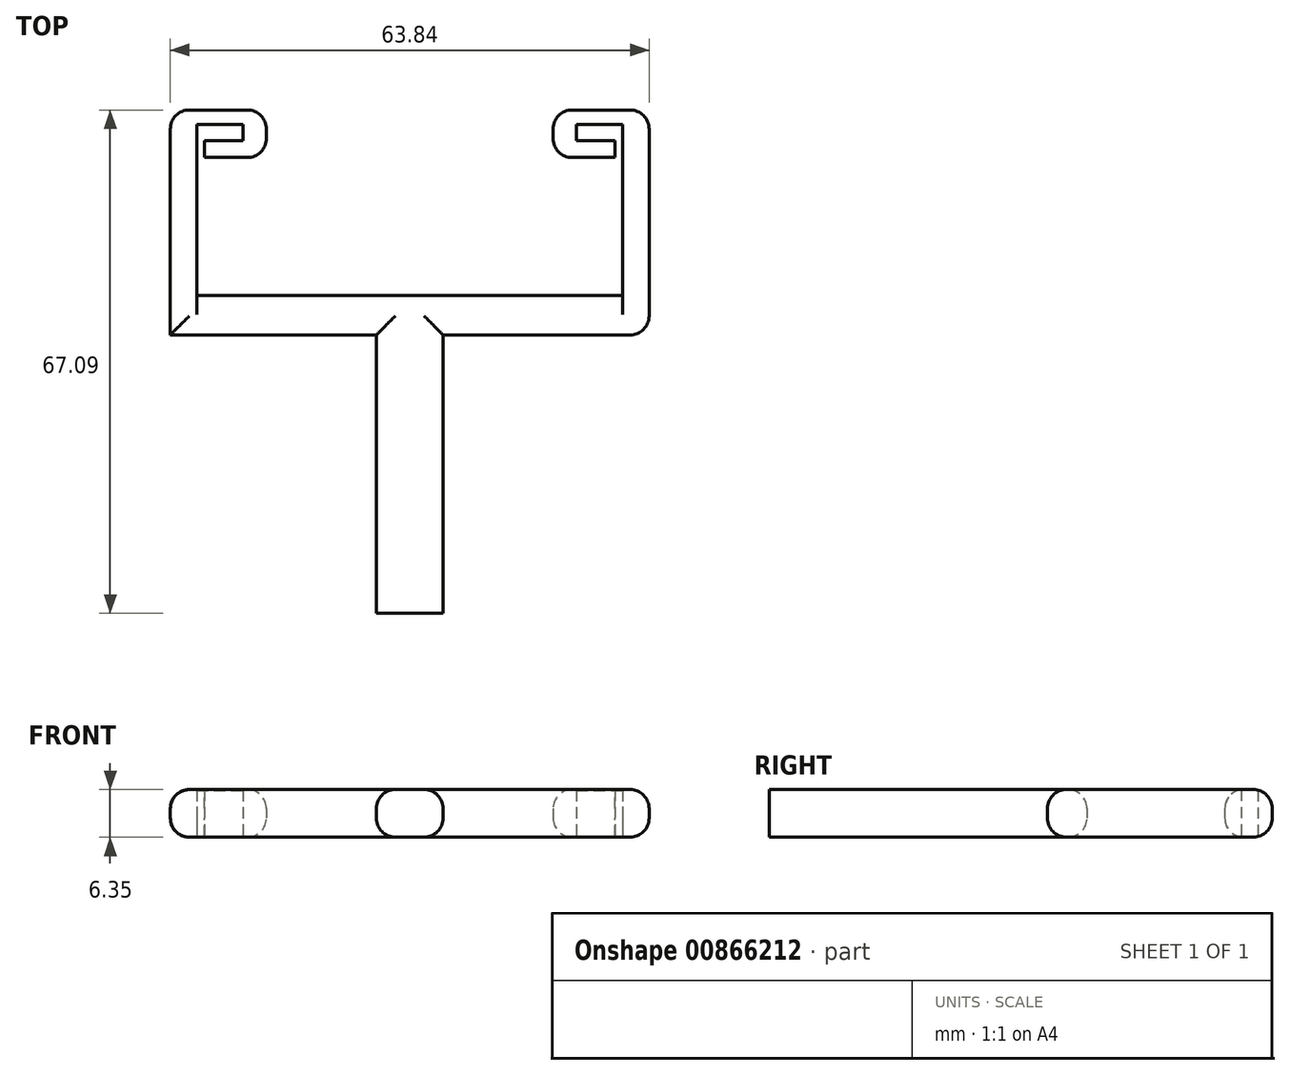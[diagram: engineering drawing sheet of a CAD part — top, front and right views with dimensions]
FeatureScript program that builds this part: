
annotation { "Feature Type Name" : "Feature", "Feature Type Description" : "" }
export const myFeature = defineFeature(function(context is Context, id is Id, definition is map)
    precondition{}
    {
        {
            var Q0;
            Q0=qCreatedBy(makeId("Top.planeOp"),FACE);
            var sketch = newSketch(context, id + "F0", { "sketchPlane" : qUnion([Q0])});
            skLineSegment(sketch, "E0.bottom", {"start": v(0, -33.38) * mm, "end": v(-4.45, -33.38) * mm});
            skLineSegment(sketch, "E0.top", {"start": v(0, 9) * mm, "end": v(-4.45, 9) * mm});
            skLineSegment(sketch, "E0.right", {"start": v(-4.45, -33.38) * mm, "end": v(-4.45, 3.72) * mm});
            skLineSegment(sketch, "E1.bottom", {"start": v(-4.45, 9) * mm, "end": v(-28.38, 9) * mm});
            skLineSegment(sketch, "E1.top", {"start": v(-4.45, 3.72) * mm, "end": v(-31.92, 3.72) * mm});
            skLineSegment(sketch, "E1.right", {"start": v(-31.92, 9) * mm, "end": v(-31.92, 3.72) * mm});
            skLineSegment(sketch, "E2.top", {"start": v(-31.92, 33.7) * mm, "end": v(-28.38, 33.7) * mm});
            skLineSegment(sketch, "E2.left", {"start": v(-31.92, 9) * mm, "end": v(-31.92, 33.7) * mm});
            skLineSegment(sketch, "E2.right", {"start": v(-28.38, 9) * mm, "end": v(-28.38, 31.8) * mm});
            skLineSegment(sketch, "E3.bottom", {"start": v(-19.1, 33.7) * mm, "end": v(-28.38, 33.7) * mm});
            skLineSegment(sketch, "E3.top", {"start": v(-22.24, 31.8) * mm, "end": v(-28.38, 31.8) * mm});
            skLineSegment(sketch, "E3.left", {"start": v(-19.1, 33.7) * mm, "end": v(-19.1, 31.8) * mm});
            skLineSegment(sketch, "E4.top", {"start": v(-19.1, 27.38) * mm, "end": v(-22.24, 27.38) * mm});
            skLineSegment(sketch, "E4.left", {"start": v(-19.1, 31.8) * mm, "end": v(-19.1, 27.38) * mm});
            skLineSegment(sketch, "E4.right", {"start": v(-22.24, 31.8) * mm, "end": v(-22.24, 29.6) * mm});
            skLineSegment(sketch, "E5.bottom", {"start": v(-27.34, 27.38) * mm, "end": v(-22.24, 27.38) * mm});
            skLineSegment(sketch, "E5.top", {"start": v(-27.34, 29.6) * mm, "end": v(-22.24, 29.6) * mm});
            skLineSegment(sketch, "E5.left", {"start": v(-27.34, 27.38) * mm, "end": v(-27.34, 29.6) * mm});
            skLineSegment(sketch, "E6.MirrorCS", {"start": v(4.45, -33.38) * mm, "end": v(4.45, 3.72) * mm});
            skLineSegment(sketch, "E7.MirrorCS", {"start": v(0, 9) * mm, "end": v(4.45, 9) * mm});
            skLineSegment(sketch, "E8.MirrorCS", {"start": v(4.45, 3.72) * mm, "end": v(31.92, 3.72) * mm});
            skLineSegment(sketch, "E9.MirrorCS", {"start": v(4.45, 9) * mm, "end": v(28.38, 9) * mm});
            skLineSegment(sketch, "E10.MirrorCS", {"start": v(28.38, 9) * mm, "end": v(28.38, 31.8) * mm});
            skLineSegment(sketch, "E11.MirrorCS", {"start": v(31.92, 9) * mm, "end": v(31.92, 33.7) * mm});
            skLineSegment(sketch, "E12.MirrorCS", {"start": v(19.1, 33.7) * mm, "end": v(28.38, 33.7) * mm});
            skLineSegment(sketch, "E13.MirrorCS", {"start": v(31.92, 33.7) * mm, "end": v(28.38, 33.7) * mm});
            skLineSegment(sketch, "E14.MirrorCS", {"start": v(19.1, 31.8) * mm, "end": v(19.1, 27.38) * mm});
            skLineSegment(sketch, "E15.MirrorCS", {"start": v(22.24, 31.8) * mm, "end": v(28.38, 31.8) * mm});
            skLineSegment(sketch, "E16.MirrorCS", {"start": v(27.34, 29.6) * mm, "end": v(22.24, 29.6) * mm});
            skLineSegment(sketch, "E17.MirrorCS", {"start": v(27.34, 27.38) * mm, "end": v(27.34, 29.6) * mm});
            skLineSegment(sketch, "E18.MirrorCS", {"start": v(27.34, 27.38) * mm, "end": v(22.24, 27.38) * mm});
            skLineSegment(sketch, "E19.MirrorCS", {"start": v(19.1, 27.38) * mm, "end": v(22.24, 27.38) * mm});
            skLineSegment(sketch, "E20.MirrorCS", {"start": v(22.24, 31.8) * mm, "end": v(22.24, 29.6) * mm});
            skLineSegment(sketch, "E21.MirrorCS", {"start": v(19.1, 33.7) * mm, "end": v(19.1, 31.8) * mm});
            skLineSegment(sketch, "E22.MirrorCS", {"start": v(31.92, 9) * mm, "end": v(31.92, 3.72) * mm});
            skLineSegment(sketch, "E23.MirrorCS", {"start": v(0, -33.38) * mm, "end": v(4.45, -33.38) * mm});
            skSolve(sketch);
        }
        {
            var Q0;
            Q0=makeQuery(id+"F0.imprint","IMPRINT",FACE,{"disambiguationData":[TD([[makeQuery(id+"F0.imprint","IMPRINT",EDGE,{"derivedFrom":sQuery(id+"F0.wireOp",EDGE,"E0.bottom")}),-1.0]])]});
            extrude(context, id + "F1", {"entities" : qUnion([Q0]), "depth" : 6.35 * mm, "offsetDistance" : 25.4 * mm});
        }
        {
            var Q0;
            Q0=makeQuery(id+"F1.opExtrude","CAP_EDGE",EDGE,{"disambiguationData":[OSD([sQuery(id+"F0.wireOp",EDGE,"E12.MirrorCS"),sQuery(id+"F0.wireOp",EDGE,"E13.MirrorCS")])],"isStart":true});
            var Q1;
            Q1=makeQuery(id+"F1.opExtrude","CAP_EDGE",EDGE,{"disambiguationData":[OSD([sQuery(id+"F0.wireOp",EDGE,"E12.MirrorCS"),sQuery(id+"F0.wireOp",EDGE,"E13.MirrorCS")])],"isStart":false});
            var Q2;
            Q2=makeQuery(id+"F1.opExtrude","CAP_EDGE",EDGE,{"disambiguationData":[OSD([sQuery(id+"F0.wireOp",EDGE,"E18.MirrorCS"),sQuery(id+"F0.wireOp",EDGE,"E19.MirrorCS")])],"isStart":true});
            var Q3;
            Q3=makeQuery(id+"F1.opExtrude","CAP_EDGE",EDGE,{"disambiguationData":[OSD([sQuery(id+"F0.wireOp",EDGE,"E14.MirrorCS"),sQuery(id+"F0.wireOp",EDGE,"E21.MirrorCS")])],"isStart":true});
            var Q4;
            Q4=makeQuery(id+"F1.opExtrude","CAP_EDGE",EDGE,{"disambiguationData":[OSD([sQuery(id+"F0.wireOp",EDGE,"E14.MirrorCS"),sQuery(id+"F0.wireOp",EDGE,"E21.MirrorCS")])],"isStart":false});
            var Q5;
            Q5=makeQuery(id+"F1.opExtrude","SWEPT_EDGE",EDGE,{"disambiguationData":[OSD([sQuery(id+"F0.wireOp",EDGE,"E14.MirrorCS"),sQuery(id+"F0.wireOp",EDGE,"E19.MirrorCS")])]});
            var Q6;
            Q6=makeQuery(id+"F1.opExtrude","CAP_EDGE",EDGE,{"disambiguationData":[OSD([sQuery(id+"F0.wireOp",EDGE,"E18.MirrorCS"),sQuery(id+"F0.wireOp",EDGE,"E19.MirrorCS")])],"isStart":false});
            fillet(context, id + "F2", {"entities" : qUnion([Q0, Q1, Q2, Q3, Q4, Q5, Q6]), "radius" : 2.54 * mm, "tangentPropagation" : true, "allowEdgeOverflow" : false});
        }
        {
            var Q0;
            Q0=makeQuery(id+"F1.opExtrude","CAP_EDGE",EDGE,{"disambiguationData":[OSD([sQuery(id+"F0.wireOp",EDGE,"E4.top"),sQuery(id+"F0.wireOp",EDGE,"E5.bottom")])],"isStart":true});
            var Q1;
            Q1=makeQuery(id+"F1.opExtrude","CAP_EDGE",EDGE,{"disambiguationData":[OSD([sQuery(id+"F0.wireOp",EDGE,"E4.top"),sQuery(id+"F0.wireOp",EDGE,"E5.bottom")])],"isStart":false});
            var Q2;
            Q2=makeQuery(id+"F1.opExtrude","CAP_EDGE",EDGE,{"disambiguationData":[OSD([sQuery(id+"F0.wireOp",EDGE,"E3.left"),sQuery(id+"F0.wireOp",EDGE,"E4.left")])],"isStart":false});
            var Q3;
            Q3=makeQuery(id+"F1.opExtrude","CAP_EDGE",EDGE,{"disambiguationData":[OSD([sQuery(id+"F0.wireOp",EDGE,"E3.left"),sQuery(id+"F0.wireOp",EDGE,"E4.left")])],"isStart":true});
            var Q4;
            Q4=makeQuery(id+"F1.opExtrude","CAP_EDGE",EDGE,{"disambiguationData":[OSD([sQuery(id+"F0.wireOp",EDGE,"E2.top"),sQuery(id+"F0.wireOp",EDGE,"E3.bottom")])],"isStart":false});
            var Q5;
            Q5=makeQuery(id+"F1.opExtrude","SWEPT_FACE",FACE,{"disambiguationData":[OSD([sQuery(id+"F0.wireOp",EDGE,"E2.top"),sQuery(id+"F0.wireOp",EDGE,"E3.bottom")])]});
            var Q6;
            Q6=makeQuery(id+"F1.opExtrude","SWEPT_EDGE",EDGE,{"disambiguationData":[OSD([sQuery(id+"F0.wireOp",EDGE,"E12.MirrorCS"),sQuery(id+"F0.wireOp",EDGE,"E21.MirrorCS")])]});
            var Q7;
            Q7=makeQuery(id+"F1.opExtrude","SWEPT_EDGE",EDGE,{"disambiguationData":[OSD([sQuery(id+"F0.wireOp",EDGE,"E11.MirrorCS"),sQuery(id+"F0.wireOp",EDGE,"E13.MirrorCS")])]});
            fillet(context, id + "F3", {"entities" : qUnion([Q0, Q1, Q2, Q3, Q4, Q5, Q6, Q7]), "radius" : 2.54 * mm, "tangentPropagation" : true, "allowEdgeOverflow" : false});
        }
        {
            var Q0;
            Q0=makeQuery(id+"F1.opExtrude","CAP_EDGE",EDGE,{"disambiguationData":[OSD([sQuery(id+"F0.wireOp",EDGE,"E1.right"),sQuery(id+"F0.wireOp",EDGE,"E2.left")])],"isStart":false});
            var Q1;
            Q1=makeQuery(id+"F1.opExtrude","CAP_EDGE",EDGE,{"disambiguationData":[OSD([sQuery(id+"F0.wireOp",EDGE,"E1.right"),sQuery(id+"F0.wireOp",EDGE,"E2.left")])],"isStart":true});
            var Q2;
            Q2=makeQuery(id+"F1.opExtrude","CAP_EDGE",EDGE,{"disambiguationData":[OSD([sQuery(id+"F0.wireOp",EDGE,"E0.top"),sQuery(id+"F0.wireOp",EDGE,"E1.bottom"),sQuery(id+"F0.wireOp",EDGE,"E7.MirrorCS"),sQuery(id+"F0.wireOp",EDGE,"E9.MirrorCS")])],"isStart":false});
            var Q3;
            Q3=makeQuery(id+"F1.opExtrude","CAP_EDGE",EDGE,{"disambiguationData":[OSD([sQuery(id+"F0.wireOp",EDGE,"E1.top")])],"isStart":false});
            var Q4;
            Q4=makeQuery(id+"F1.opExtrude","CAP_EDGE",EDGE,{"disambiguationData":[OSD([sQuery(id+"F0.wireOp",EDGE,"E8.MirrorCS")])],"isStart":false});
            var Q5;
            Q5=makeQuery(id+"F1.opExtrude","CAP_EDGE",EDGE,{"disambiguationData":[OSD([sQuery(id+"F0.wireOp",EDGE,"E0.top"),sQuery(id+"F0.wireOp",EDGE,"E1.bottom"),sQuery(id+"F0.wireOp",EDGE,"E7.MirrorCS"),sQuery(id+"F0.wireOp",EDGE,"E9.MirrorCS")])],"isStart":true});
            var Q6;
            Q6=makeQuery(id+"F1.opExtrude","CAP_EDGE",EDGE,{"disambiguationData":[OSD([sQuery(id+"F0.wireOp",EDGE,"E1.top")])],"isStart":true});
            fillet(context, id + "F4", {"entities" : qUnion([Q0, Q1, Q2, Q3, Q4, Q5, Q6]), "radius" : 2.54 * mm, "tangentPropagation" : true, "allowEdgeOverflow" : false});
        }
        {
            var Q0;
            Q0=makeQuery(id+"F1.opExtrude","CAP_EDGE",EDGE,{"disambiguationData":[OSD([sQuery(id+"F0.wireOp",EDGE,"E0.right")])],"isStart":true});
            var Q1;
            Q1=makeQuery(id+"F1.opExtrude","CAP_EDGE",EDGE,{"disambiguationData":[OSD([sQuery(id+"F0.wireOp",EDGE,"E6.MirrorCS")])],"isStart":true});
            fillet(context, id + "F5", {"entities" : qUnion([Q0, Q1]), "radius" : 2.54 * mm, "tangentPropagation" : true, "allowEdgeOverflow" : false});
        }
        {
            var Q0;
            Q0=makeQuery(id+"F1.opExtrude","CAP_EDGE",EDGE,{"disambiguationData":[OSD([sQuery(id+"F0.wireOp",EDGE,"E0.right")])],"isStart":false});
            var Q1;
            Q1=makeQuery(id+"F1.opExtrude","CAP_EDGE",EDGE,{"disambiguationData":[OSD([sQuery(id+"F0.wireOp",EDGE,"E6.MirrorCS")])],"isStart":false});
            fillet(context, id + "F6", {"entities" : qUnion([Q0, Q1]), "radius" : 2.54 * mm, "tangentPropagation" : true, "allowEdgeOverflow" : false});
        }
        {
            var Q0;
            Q0=makeQuery(id+"F1.opExtrude","SWEPT_EDGE",EDGE,{"disambiguationData":[OSD([sQuery(id+"F0.wireOp",EDGE,"E4.top"),sQuery(id+"F0.wireOp",EDGE,"E4.left")])]});
            fillet(context, id + "F7", {"entities" : qUnion([Q0]), "radius" : 2.54 * mm, "tangentPropagation" : true, "allowEdgeOverflow" : false});
        }
    });
